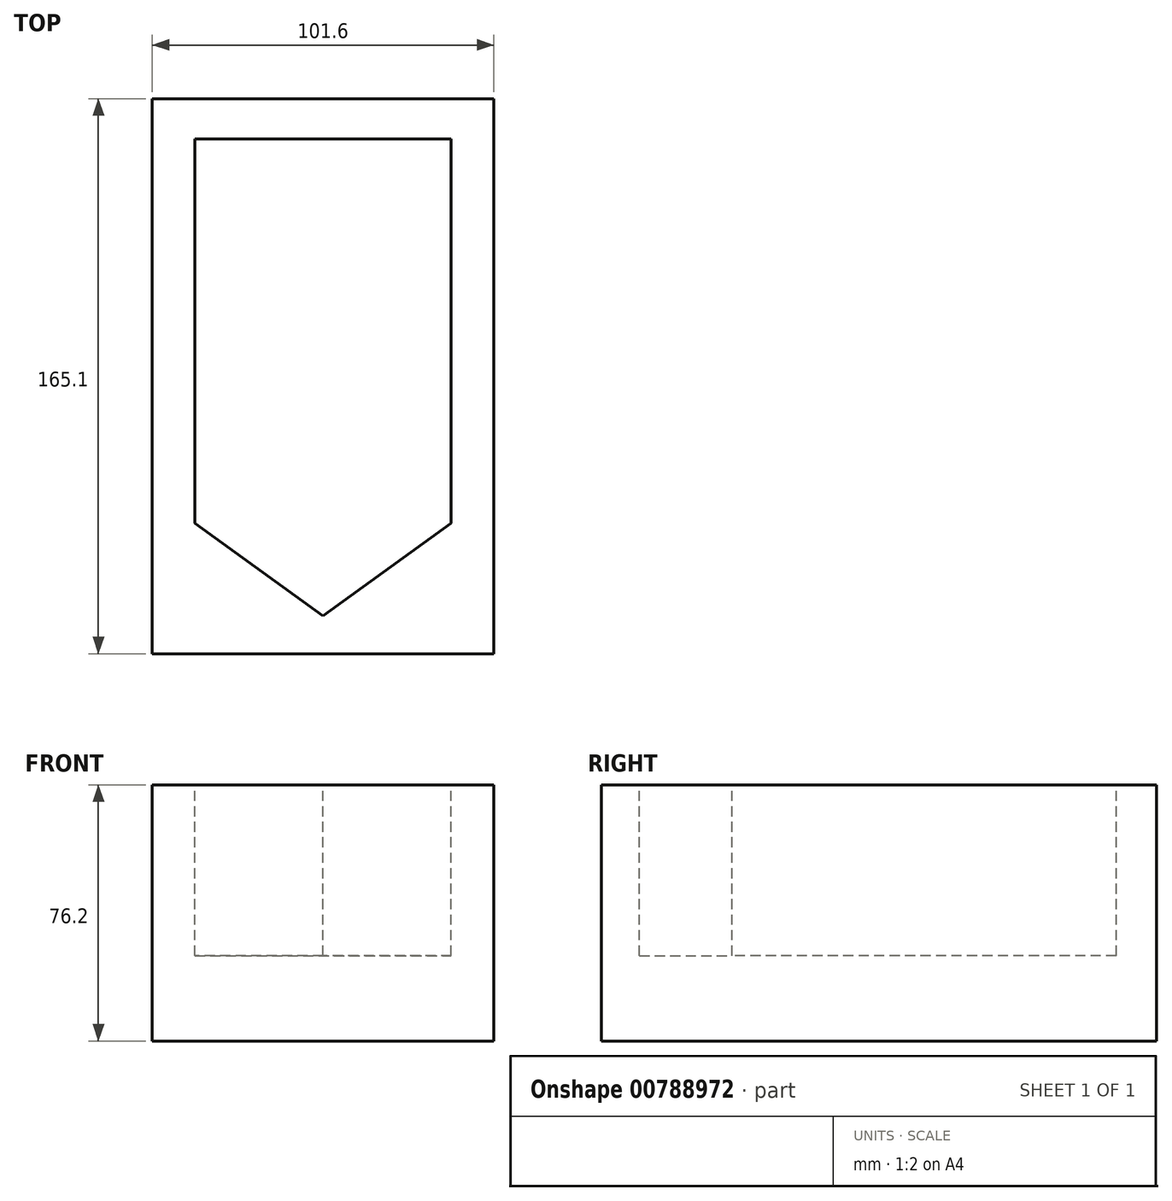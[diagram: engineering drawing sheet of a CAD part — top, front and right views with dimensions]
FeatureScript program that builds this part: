
annotation { "Feature Type Name" : "Feature", "Feature Type Description" : "" }
export const myFeature = defineFeature(function(context is Context, id is Id, definition is map)
    precondition{}
    {
        {
            var Q0;
            Q0=qCreatedBy(makeId("Top.planeOp"),FACE);
            var sketch = newSketch(context, id + "F0", { "sketchPlane" : qUnion([Q0])});
            skLineSegment(sketch, "E0", {"start": v(0, 0) * mm, "end": v(0, 165.1) * mm});
            skLineSegment(sketch, "E1", {"start": v(0, 0) * mm, "end": v(101.6, 0) * mm});
            skLineSegment(sketch, "E2", {"start": v(101.6, 0) * mm, "end": v(101.6, 165.1) * mm});
            skLineSegment(sketch, "E3", {"start": v(101.6, 165.1) * mm, "end": v(0, 165.1) * mm});
            skSolve(sketch);
        }
        {
            var Q0;
            Q0 = qSketchRegion(id + "F0", true);
            var Q1;
            Q1=makeQuery(id+"F0.imprint","IMPRINT",FACE,{"disambiguationData":[TD([[makeQuery(id+"F0.imprint","IMPRINT",EDGE,{"derivedFrom":sQuery(id+"F0.wireOp",EDGE,"LVKaI2aE-FhHV-D4Oa-oDQh-NGdHOsHOuphO")}),-1.0]])]});
            extrude(context, id + "F1", {"entities" : qUnion([Q0, Q1]), "depth" : 76.2 * mm, "offsetDistance" : 25 * mm});
        }
        {
            var Q0;
            Q0=makeQuery(id+"F1.opExtrude","CAP_FACE",FACE,{"disambiguationData":[OSD([sQuery(id+"F0.wireOp",EDGE,"E0"),sQuery(id+"F0.wireOp",EDGE,"E1"),sQuery(id+"F0.wireOp",EDGE,"E2"),sQuery(id+"F0.wireOp",EDGE,"E3")])],"isStart":false});
            var sketch = newSketch(context, id + "F2", { "sketchPlane" : qUnion([Q0])});
            skLineSegment(sketch, "E4", {"start": v(0, 165.1) * mm, "end": v(0, 0) * mm});
            skLineSegment(sketch, "E5", {"start": v(50.8, 11.28) * mm, "end": v(12.7, 38.8) * mm});
            skPoint(sketch, "E5.startSnap0", {"position": v(50.8, 0) * mm});
            skLineSegment(sketch, "E6", {"start": v(12.7, 38.8) * mm, "end": v(12.7, 153.1) * mm});
            skLineSegment(sketch, "E7", {"start": v(12.7, 153.1) * mm, "end": v(88.9, 153.1) * mm});
            skLineSegment(sketch, "E8", {"start": v(88.9, 153.1) * mm, "end": v(88.9, 38.8) * mm});
            skLineSegment(sketch, "E9", {"start": v(88.9, 38.8) * mm, "end": v(50.8, 11.28) * mm});
            skLineSegment(sketch, "E10", {"start": v(0, 165.1) * mm, "end": v(12.7, 165.1) * mm});
            skLineSegment(sketch, "E11", {"start": v(101.6, 165.1) * mm, "end": v(88.9, 165.1) * mm});
            skLineSegment(sketch, "E12", {"start": v(50.8, 165.1) * mm, "end": v(50.8, 153.1) * mm});
            skLineSegment(sketch, "E13", {"start": v(50.8, 11.28) * mm, "end": v(50.8, 0) * mm});
            skSolve(sketch);
        }
        {
            var Q0;
            Q0 = qSketchRegion(id + "F2", true);
            extrude(context, id + "F3", {"entities" : qUnion([Q0]), "operationType" : NewBodyOperationType.REMOVE, "oppositeDirection" : true, "depth" : 50.8 * mm, "offsetDistance" : 25 * mm});
        }
    });
